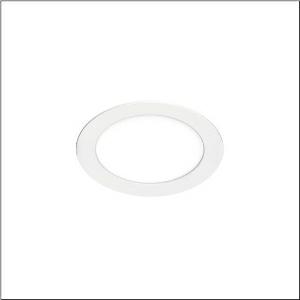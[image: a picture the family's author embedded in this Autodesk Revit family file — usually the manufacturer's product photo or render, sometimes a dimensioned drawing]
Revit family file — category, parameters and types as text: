
# Revit family: lunis_41_flat_51dr107fhca
name_source: partatom
category: Lighting Fixtures
units: mm (PartAtom-declared; Revit-internal decimal feet)

## family parameters
Cut with Voids When Loaded = No
Host = Face
Light Source = No
Part Type = Normal
Room Calculation Point = No
Round Connector Dimension = Use Diameter
Shared = No

## types (1)
- --- (1 x LED, 2160 lm, 22 W, 5700K)
    Apparent Load = 22 VA
    CIE Flux Codes = 49 80 96 100 100
    Color Rendering = 80
    Color Temperature = 5700K
    Default Elevation = 1800 mm
    Description = Lunis 41,  Flat, downlight, light emission: direct distribution, LED rated luminous flux: 2.160lm, light colour: 840/857, control gear: ECG, mains connection: 230V, AC, 50/60Hz, housing, round, of aluminium, coated, traffic white (RAL 9016), diameter: 225mm, protection rating (complete): IP20, protection rating (on room side): IP44, insulation class (complete): insulation class II (safety insulation), certification: CE, permissible ambient temperature for indoor applications: -20..+40°C, packaging unit: 1 piece
    Height = 0 mm  [stored 0 ft]
    Lamp = 1 x LED
    Lamp Light Flux = 2160 lm
    Lamp Power = 22 W
    Lamp count = 1
    Length = 225 mm
    Luminous efficacy = 98 lm/W
    Manufacturer = Siteco
    ModVariant = No
    Model = 51DR107FHCA
    Mounting Place = Ceiling
    Mounting Type = Recessed
    Number of Poles = 1
    OnlyDefault = Yes
    Power Factor = 1
    Product Name = Lunis 41 Flat
    Product group = downlight
    ProductGroupID = 400
    Protection Class = Protection class II
    Protection Degree = IP 20
    RLX_Detail_Level = 1
    RLX_Emergency_Light_Flux = 0 lm
    RLX_Emergency_Type = 0
    RLX_Emergency_Type_DB = No
    RlxData = <blob elided: 22057 chars, md5=9b062f3b>
    Socket = socket
    Standby Power = 0 W
    System Light Flux = 2160 lm
    System Power = 22 W
    Type Comments = factory setting: colour temperature 5700K
    Type Image = l_1340923.jpg
    URL = http://relux.com
    VarID = @adj_195566
    Voltage = 0 V
    Weight = 0.00 kg
    Width = 0 mm  [stored 0 ft]

note: [stored X ft] marks values corroborated as IEEE doubles in the binary element streams (Revit-internal decimal feet)

## geometry (parser evidence)
native form markers: Blend x4, Sweep x10
no freeform markers — native parametric forms only
